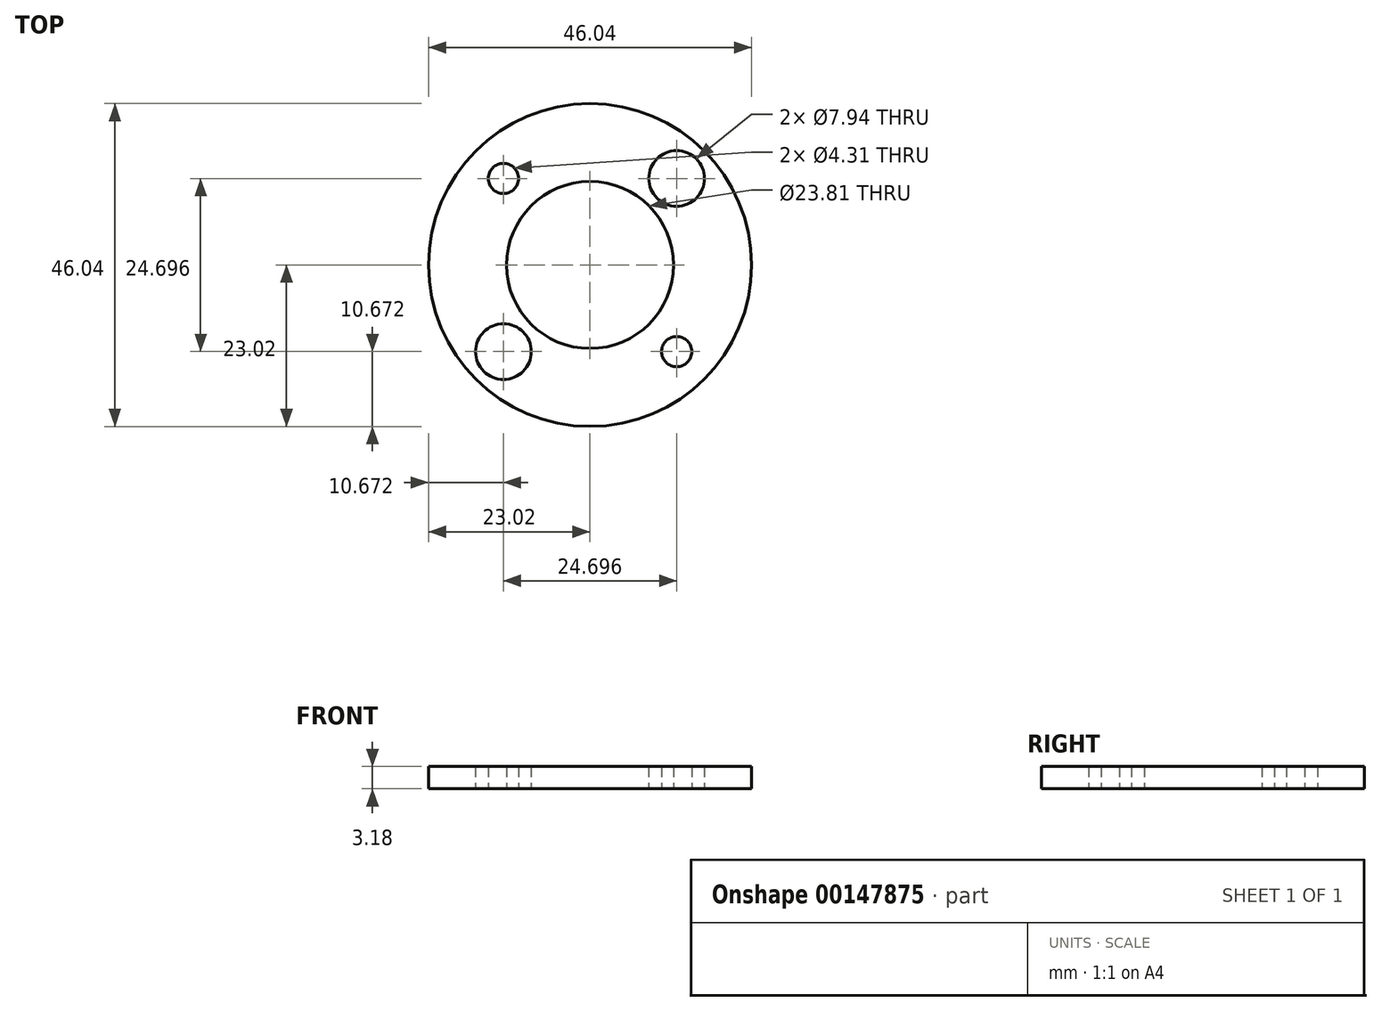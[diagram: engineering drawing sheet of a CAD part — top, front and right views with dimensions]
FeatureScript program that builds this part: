
annotation { "Feature Type Name" : "Feature", "Feature Type Description" : "" }
export const myFeature = defineFeature(function(context is Context, id is Id, definition is map)
    precondition{}
    {
        {
            var Q0;
            Q0=qCreatedBy(makeId("Top.planeOp"),FACE);
            var sketch = newSketch(context, id + "F0", { "sketchPlane" : qUnion([Q0])});
            skCircle(sketch, "E0", {"center": v(0, 0) * mm, "radius": 23.02 * mm});
            skCircle(sketch, "E1", {"center": v(0, 0) * mm, "radius": 11.9 * mm});
            skLineSegment(sketch, "E2.bottom", {"start": v(-12.35, 12.35) * mm, "end": v(12.35, 12.35) * mm, "construction": true});
            skLineSegment(sketch, "E2.top", {"start": v(-12.35, -12.35) * mm, "end": v(12.35, -12.35) * mm, "construction": true});
            skLineSegment(sketch, "E2.left", {"start": v(-12.35, 12.35) * mm, "end": v(-12.35, -12.35) * mm, "construction": true});
            skLineSegment(sketch, "E2.right", {"start": v(12.35, 12.35) * mm, "end": v(12.35, -12.35) * mm, "construction": true});
            skCircle(sketch, "E3", {"center": v(-12.35, 12.35) * mm, "radius": 5.56 * mm, "construction": true});
            skCircle(sketch, "E4", {"center": v(12.35, 12.35) * mm, "radius": 3.97 * mm});
            skCircle(sketch, "E5", {"center": v(-12.35, 12.35) * mm, "radius": 2.15 * mm});
            skCircle(sketch, "E6", {"center": v(-12.35, -12.35) * mm, "radius": 3.97 * mm});
            skCircle(sketch, "E7", {"center": v(12.35, -12.35) * mm, "radius": 2.15 * mm});
            skSolve(sketch);
        }
        {
            var Q0;
            Q0=qSketchRegion(id+"F0",true);
            extrude(context, id + "F1", {"entities" : qUnion([Q0]), "depth" : 3.17 * mm});
        }
    });
